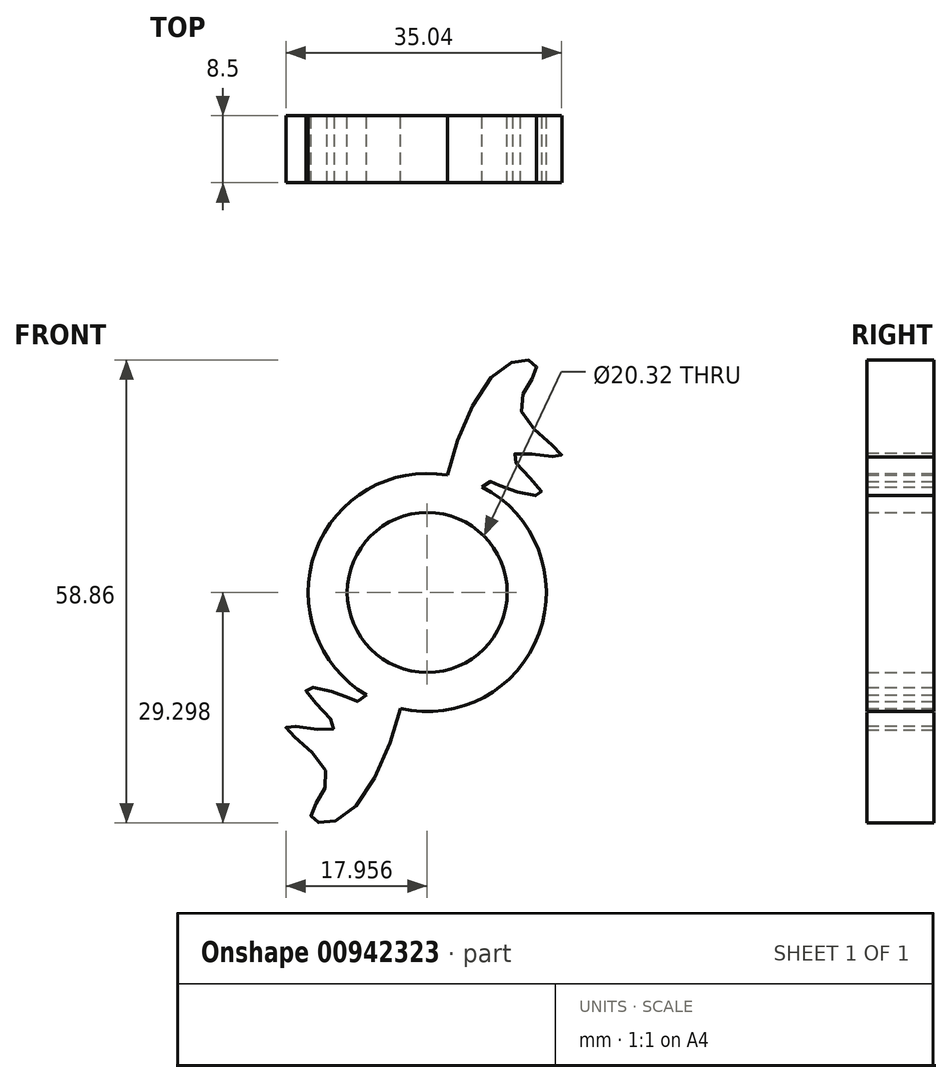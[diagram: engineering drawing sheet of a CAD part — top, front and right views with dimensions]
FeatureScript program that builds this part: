
annotation { "Feature Type Name" : "Feature", "Feature Type Description" : "" }
export const myFeature = defineFeature(function(context is Context, id is Id, definition is map)
    precondition{}
    {
        {
            var Q0;
            Q0=qCreatedBy(makeId("Front.planeOp"),FACE);
            var sketch = newSketch(context, id + "F0", { "sketchPlane" : qUnion([Q0])});
            skFitSpline(sketch, "E0", {"points": [v(-41.03, 33.66) * mm, v(-47.49, 15.39) * mm, v(-42.46, 19.45) * mm, v(-40.9, 19.2) * mm, v(-35.42, 18.15) * mm, v(-39.07, 22.97) * mm, v(-32.95, 22.84) * mm, v(-38.03, 28.7) * mm, v(-36.08, 34.18) * mm, v(-41.03, 33.66) * mm]});
            skCircle(sketch, "E1", {"center": v(-49.97, 5.54) * mm, "radius": 15.13 * mm});
            skPoint(sketch, "E2.center", {"position": v(0, 0) * mm});
            skFitSpline(sketch, "E3", {"points": [v(-59.8, -22.32) * mm, v(-53.31, -4.06) * mm, v(-58.36, -8.12) * mm, v(-59.93, -7.86) * mm, v(-65.4, -6.81) * mm, v(-61.75, -11.63) * mm, v(-67.87, -11.5) * mm, v(-62.8, -17.37) * mm, v(-64.75, -22.84) * mm, v(-59.8, -22.32) * mm]});
            skCircle(sketch, "E4", {"center": v(-49.97, 5.54) * mm, "radius": 10.16 * mm});
            skSolve(sketch);
        }
        {
            var Q0;
            Q0 = qSketchRegion(id + "F0", true);
            extrude(context, id + "F1", {"entities" : qUnion([Q0]), "depth" : 8.5 * mm, "offsetDistance" : 25.4 * mm});
        }
    });
